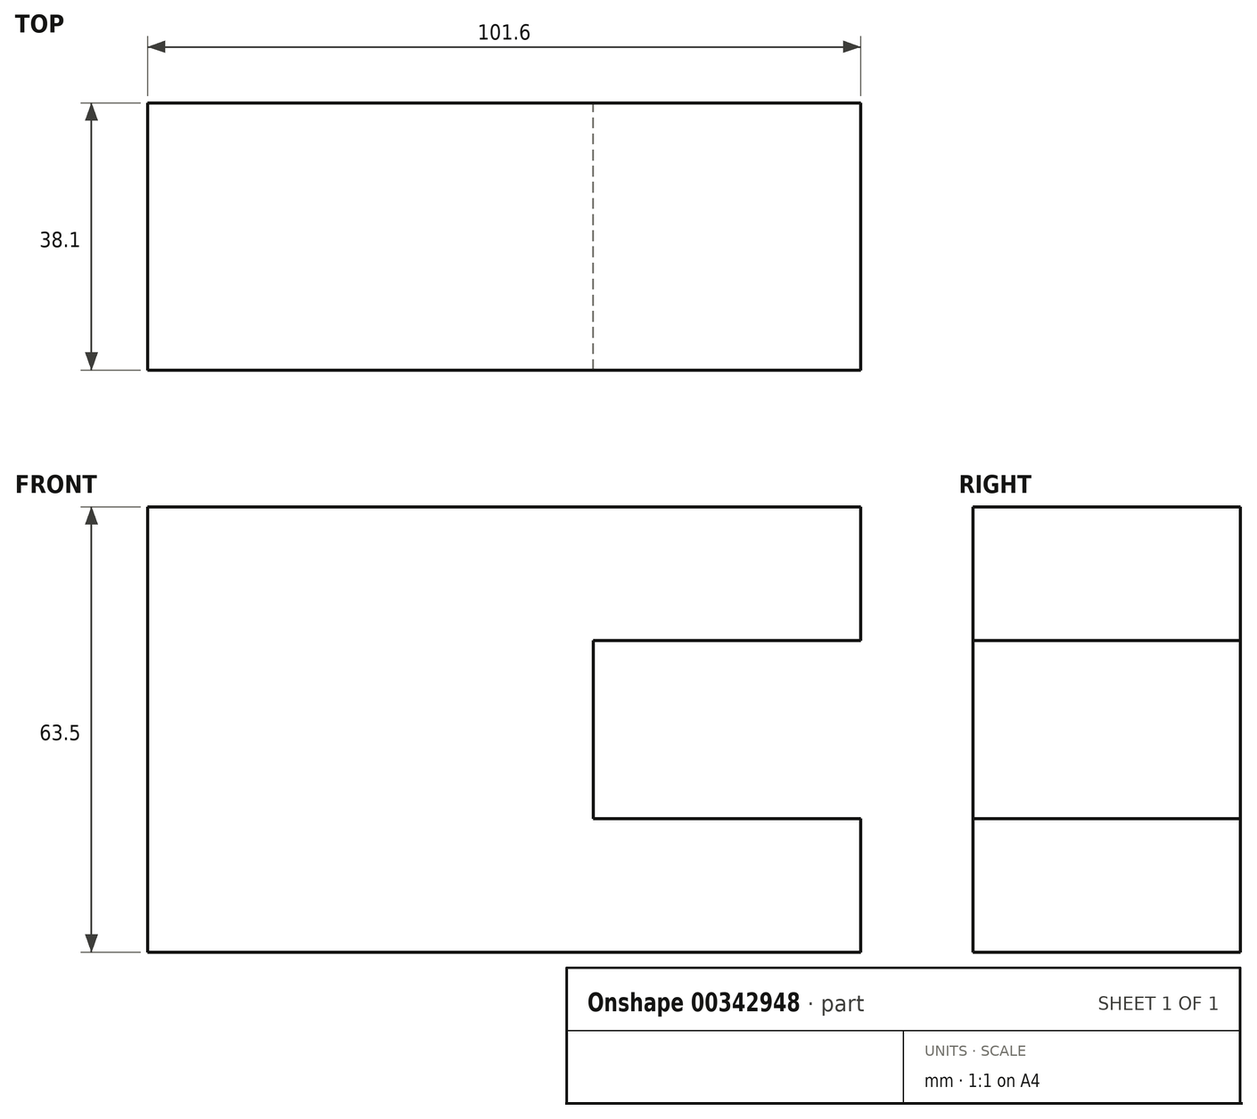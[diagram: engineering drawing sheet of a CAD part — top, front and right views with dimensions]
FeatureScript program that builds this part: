
annotation { "Feature Type Name" : "Feature", "Feature Type Description" : "" }
export const myFeature = defineFeature(function(context is Context, id is Id, definition is map)
    precondition{}
    {
        {
            var Q0;
            Q0=qCreatedBy(makeId("Front.planeOp"),FACE);
            var sketch = newSketch(context, id + "F0", { "sketchPlane" : qUnion([Q0])});
            skLineSegment(sketch, "E0", {"start": v(-63.5, 38.3) * mm, "end": v(-63.5, -25.2) * mm});
            skLineSegment(sketch, "E1", {"start": v(-63.5, 38.3) * mm, "end": v(38.1, 38.3) * mm});
            skLineSegment(sketch, "E2", {"start": v(-63.5, -25.2) * mm, "end": v(38.1, -25.2) * mm});
            skLineSegment(sketch, "E3", {"start": v(38.1, -25.2) * mm, "end": v(38.1, -6.14) * mm});
            skLineSegment(sketch, "E4", {"start": v(38.1, 38.3) * mm, "end": v(38.1, 19.26) * mm});
            skLineSegment(sketch, "E5", {"start": v(38.1, -6.14) * mm, "end": v(0, -6.14) * mm});
            skLineSegment(sketch, "E6", {"start": v(38.1, 19.26) * mm, "end": v(0, 19.26) * mm});
            skLineSegment(sketch, "E7", {"start": v(0, 19.26) * mm, "end": v(0, -6.14) * mm});
            skSolve(sketch);
        }
        {
            var Q0;
            Q0=makeQuery(id+"F0.imprint","IMPRINT",FACE,{"disambiguationData":[TD([[makeQuery(id+"F0.imprint","IMPRINT",EDGE,{"derivedFrom":sQuery(id+"F0.wireOp",EDGE,"E0")}),1.0]])]});
            extrude(context, id + "F1", {"entities" : qUnion([Q0]), "depth" : 38.1 * mm});
        }
    });
